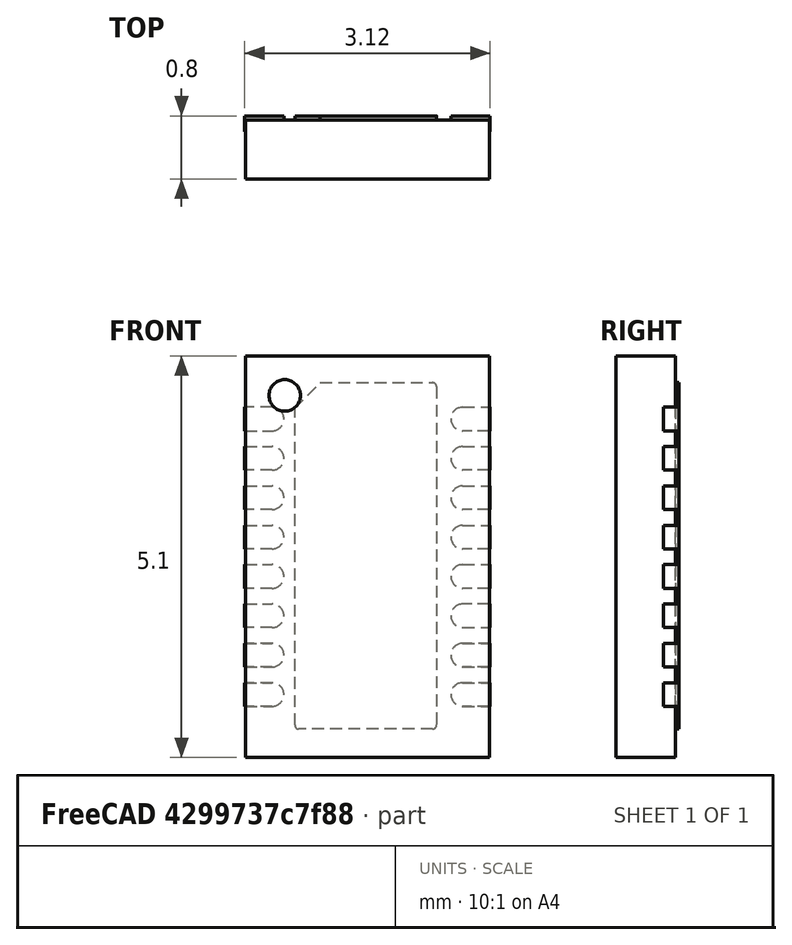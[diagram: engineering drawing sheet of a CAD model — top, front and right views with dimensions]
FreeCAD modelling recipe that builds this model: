
FCSTD DOCUMENT  (FreeCAD 0.15R4671 (Git))
Label: DFN-16-5x3mm
License: All rights reserved
LicenseURL: http://en.wikipedia.org/wiki/All_rights_reserved
objects: Part::Feature×19, Part::Fuse×18
note: 37 computed .brp shape members not serialized (recipe doc carries the construction recipe); baked Part::Feature solids carry a one-line shape summary decoded from their .brp

FEATURE [Part::Feature] Part__Feature  label="User Library-My-DFN-16-5x3-0.5"
  shape: bbox 0.5 x 0.2 x 0.3 mm, 6 faces (baked)
FEATURE [Part::Feature] Part__Feature001  label="User Library-My-DFN-16-5x3-0.006"
  shape: bbox 0.5 x 0.2 x 0.3 mm, 6 faces (baked)
FEATURE [Part::Feature] Part__Feature002  label="User Library-My-DFN-16-5x3-0.007"
  shape: bbox 0.4 x 0.05 x 0.4 mm, 4 faces (baked)
FEATURE [Part::Feature] Part__Feature003  label="User Library-My-DFN-16-5x3-0.008"
  shape: bbox 0.5 x 0.2 x 0.3 mm, 6 faces (baked)
FEATURE [Part::Feature] Part__Feature004  label="User Library-My-DFN-16-5x3-0.009"
  shape: bbox 0.5 x 0.2 x 0.3 mm, 6 faces (baked)
FEATURE [Part::Feature] Part__Feature005  label="User Library-My-DFN-16-5x3-0.010"
  shape: bbox 3.1 x 0.75 x 5.1 mm, 9 faces (baked)
FEATURE [Part::Feature] Part__Feature006  label="User Library-My-DFN-16-5x3-0.011"
  shape: bbox 0.5 x 0.2 x 0.3 mm, 6 faces (baked)
FEATURE [Part::Feature] Part__Feature007  label="User Library-My-DFN-16-5x3-0.012"
  shape: bbox 0.5 x 0.2 x 0.3 mm, 6 faces (baked)
FEATURE [Part::Feature] Part__Feature008  label="User Library-My-DFN-16-5x3-0.013"
  shape: bbox 0.5 x 0.2 x 0.3 mm, 6 faces (baked)
FEATURE [Part::Feature] Part__Feature009  label="User Library-My-DFN-16-5x3-0.014"
  shape: bbox 0.5 x 0.2 x 0.3 mm, 6 faces (baked)
FEATURE [Part::Feature] Part__Feature010  label="User Library-My-DFN-16-5x3-0.015"
  shape: bbox 0.5 x 0.2 x 0.3 mm, 6 faces (baked)
FEATURE [Part::Feature] Part__Feature011  label="User Library-My-DFN-16-5x3-0.016"
  shape: bbox 0.5 x 0.2 x 0.3 mm, 6 faces (baked)
FEATURE [Part::Feature] Part__Feature012  label="User Library-My-DFN-16-5x3-0.017"
  shape: bbox 0.5 x 0.2 x 0.3 mm, 6 faces (baked)
FEATURE [Part::Feature] Part__Feature013  label="User Library-My-DFN-16-5x3-0.018"
  shape: bbox 0.5 x 0.2 x 0.3 mm, 6 faces (baked)
FEATURE [Part::Feature] Part__Feature014  label="User Library-My-DFN-16-5x3-0.019"
  shape: bbox 0.5 x 0.2 x 0.3 mm, 6 faces (baked)
FEATURE [Part::Feature] Part__Feature015  label="User Library-My-DFN-16-5x3-0.020"
  shape: bbox 0.5 x 0.2 x 0.3 mm, 6 faces (baked)
FEATURE [Part::Feature] Part__Feature016  label="User Library-My-DFN-16-5x3-0.021"
  shape: bbox 0.5 x 0.2 x 0.3 mm, 6 faces (baked)
FEATURE [Part::Feature] Part__Feature017  label="User Library-My-DFN-16-5x3-0.022"
  shape: bbox 0.5 x 0.2 x 0.3 mm, 6 faces (baked)
FEATURE [Part::Feature] Part__Feature018  label="User Library-My-DFN-16-5x3-0.023"
  shape: bbox 1.8 x 0.2 x 4.4 mm, 10 faces (baked)
FEATURE [Part::Fuse] Fusion
  Base = -> Part__Feature
  Tool = -> Part__Feature001
FEATURE [Part::Fuse] Fusion001
  Base = -> Fusion
  Tool = -> Part__Feature002
FEATURE [Part::Fuse] Fusion002
  Base = -> Fusion001
  Tool = -> Part__Feature003
FEATURE [Part::Fuse] Fusion003
  Base = -> Fusion002
  Tool = -> Part__Feature004
FEATURE [Part::Fuse] Fusion004
  Base = -> Fusion003
  Tool = -> Part__Feature005
FEATURE [Part::Fuse] Fusion005
  Base = -> Fusion004
  Tool = -> Part__Feature006
FEATURE [Part::Fuse] Fusion006
  Base = -> Fusion005
  Tool = -> Part__Feature007
FEATURE [Part::Fuse] Fusion007
  Base = -> Fusion006
  Tool = -> Part__Feature008
FEATURE [Part::Fuse] Fusion008
  Base = -> Fusion007
  Tool = -> Part__Feature009
FEATURE [Part::Fuse] Fusion009
  Base = -> Fusion008
  Tool = -> Part__Feature010
FEATURE [Part::Fuse] Fusion010
  Base = -> Fusion009
  Tool = -> Part__Feature011
FEATURE [Part::Fuse] Fusion011
  Base = -> Fusion010
  Tool = -> Part__Feature012
FEATURE [Part::Fuse] Fusion012
  Base = -> Fusion011
  Tool = -> Part__Feature013
FEATURE [Part::Fuse] Fusion013
  Base = -> Fusion012
  Tool = -> Part__Feature014
FEATURE [Part::Fuse] Fusion014
  Base = -> Fusion013
  Tool = -> Part__Feature015
FEATURE [Part::Fuse] Fusion015
  Base = -> Fusion014
  Tool = -> Part__Feature016
FEATURE [Part::Fuse] Fusion016
  Base = -> Fusion015
  Tool = -> Part__Feature017
FEATURE [Part::Fuse] Fusion017  label="DFN-16-5x3mm"
  Base = -> Fusion016
  Tool = -> Part__Feature018
